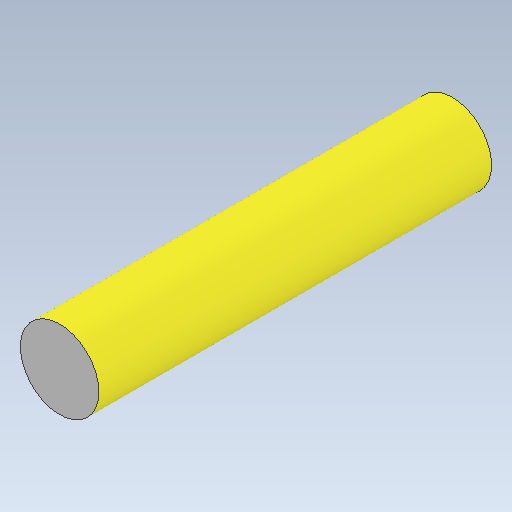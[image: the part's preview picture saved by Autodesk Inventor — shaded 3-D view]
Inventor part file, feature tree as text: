
AUTODESK INVENTOR PART (.ipt)
format: ipt  version: 2020 (Build 240168000, 168)  size: 93,184 bytes
history: native  units: in
note: dims shown in document units (in); Inventor stores cm internally (conversion verified against a paired STEP export)
features: extrude x1, sketch x1
ambient origin geometry x8: Origin, YZ Plane, XZ Plane, XY Plane, X Axis, Y Axis, Z Axis, Center Point
bodies: Solid1 (feature_tree)
feature tree (2):
  extrude  "Extrusion1"  Depth=1.9685in TaperAngle=0.0deg
  sketch  "Sketch1"  dims[d0=0.3937in d1=1.9685in d2=0.0in]
